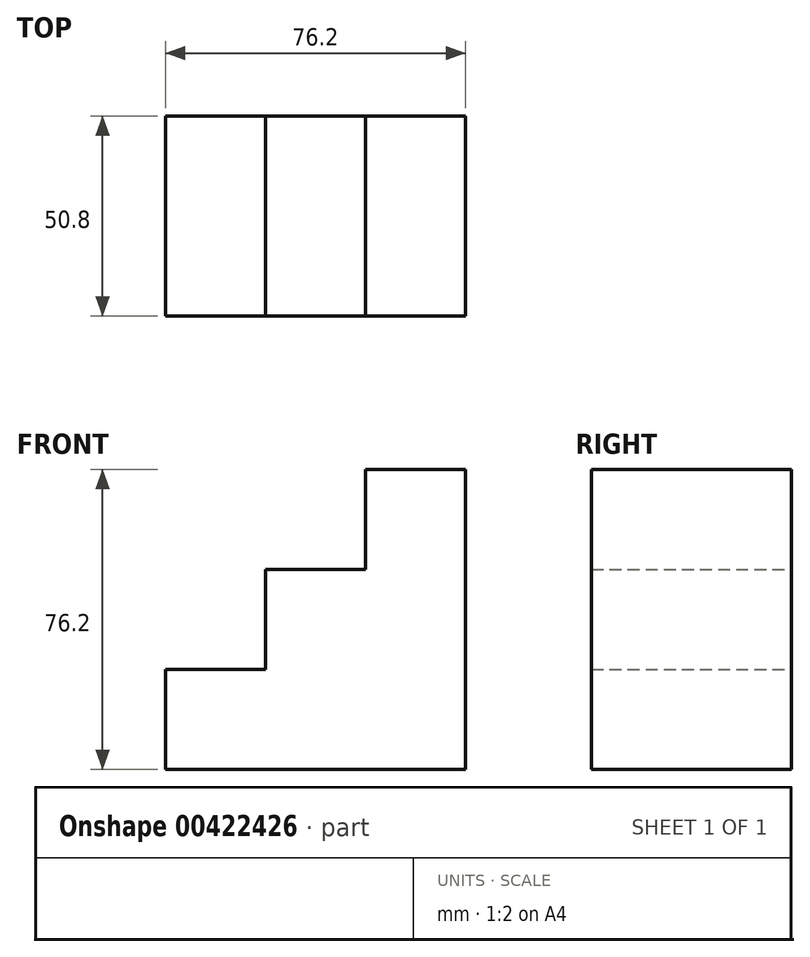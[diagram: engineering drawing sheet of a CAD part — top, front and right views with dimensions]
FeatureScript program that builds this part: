
annotation { "Feature Type Name" : "Feature", "Feature Type Description" : "" }
export const myFeature = defineFeature(function(context is Context, id is Id, definition is map)
    precondition{}
    {
        {
            var Q0;
            Q0=qCreatedBy(makeId("Front.planeOp"),FACE);
            var sketch = newSketch(context, id + "F0", { "sketchPlane" : qUnion([Q0])});
            skLineSegment(sketch, "E0", {"start": v(0, 0) * mm, "end": v(0, 76.2) * mm});
            skLineSegment(sketch, "E1", {"start": v(0, 0) * mm, "end": v(-76.2, 0) * mm});
            skLineSegment(sketch, "E2", {"start": v(0, 76.2) * mm, "end": v(-25.4, 76.2) * mm});
            skLineSegment(sketch, "E3", {"start": v(-25.4, 76.2) * mm, "end": v(-25.4, 50.8) * mm});
            skLineSegment(sketch, "E4", {"start": v(-25.4, 50.8) * mm, "end": v(-50.8, 50.8) * mm});
            skLineSegment(sketch, "E5", {"start": v(-50.8, 50.8) * mm, "end": v(-50.8, 25.4) * mm});
            skLineSegment(sketch, "E6", {"start": v(-50.8, 25.4) * mm, "end": v(-76.2, 25.4) * mm});
            skLineSegment(sketch, "E7", {"start": v(-76.2, 25.4) * mm, "end": v(-76.2, 0) * mm});
            skLineSegment(sketch, "E8", {"start": v(-25.4, -26.6) * mm, "end": v(-29.4, -27.64) * mm});
            skSolve(sketch);
        }
        {
            var Q0;
            Q0=makeQuery(id+"F0.imprint","IMPRINT",FACE,{"disambiguationData":[TD([[makeQuery(id+"F0.imprint","IMPRINT",EDGE,{"derivedFrom":sQuery(id+"F0.wireOp",EDGE,"E0")}),1.0]])]});
            extrude(context, id + "F1", {"entities" : qUnion([Q0]), "depth" : 50.8 * mm});
        }
    });
